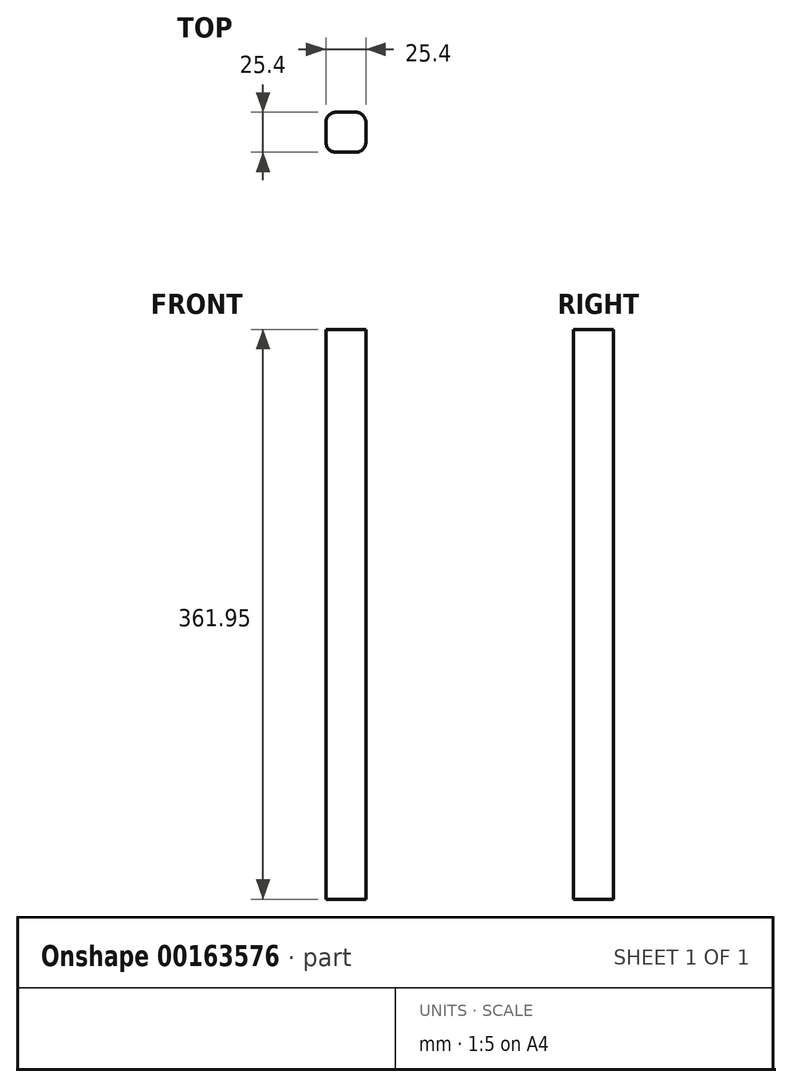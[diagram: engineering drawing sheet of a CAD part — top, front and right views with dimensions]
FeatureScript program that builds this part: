
annotation { "Feature Type Name" : "Feature", "Feature Type Description" : "" }
export const myFeature = defineFeature(function(context is Context, id is Id, definition is map)
    precondition{}
    {
        {
            var Q0;
            Q0=qCreatedBy(makeId("Top.planeOp"),FACE);
            var sketch = newSketch(context, id + "F0", { "sketchPlane" : qUnion([Q0])});
            skLineSegment(sketch, "E0.bottom", {"start": v(6.35, 12.7) * mm, "end": v(-6.35, 12.7) * mm});
            skLineSegment(sketch, "E0.top", {"start": v(6.35, -12.7) * mm, "end": v(-6.35, -12.7) * mm});
            skLineSegment(sketch, "E0.left", {"start": v(12.7, 6.35) * mm, "end": v(12.7, -6.35) * mm});
            skLineSegment(sketch, "E0.right", {"start": v(-12.7, 6.35) * mm, "end": v(-12.7, -6.35) * mm});
            skPoint(sketch, "E0.middle", {"position": v(0, 0) * mm});
            skPoint(sketch, "E1.visualSharp", {"position": v(-12.7, 12.7) * mm});
            skArc(sketch, "E1.filletArc", {"start": v(-6.35, 12.7) * mm, "mid": v(-10.84, 10.84) * mm, "end": v(-12.7, 6.35) * mm});
            skPoint(sketch, "E2.visualSharp", {"position": v(-12.7, -12.7) * mm});
            skArc(sketch, "E2.filletArc", {"start": v(-12.7, -6.35) * mm, "mid": v(-10.84, -10.84) * mm, "end": v(-6.35, -12.7) * mm});
            skPoint(sketch, "E3.visualSharp", {"position": v(12.7, -12.7) * mm});
            skArc(sketch, "E3.filletArc", {"start": v(6.35, -12.7) * mm, "mid": v(10.84, -10.84) * mm, "end": v(12.7, -6.35) * mm});
            skPoint(sketch, "E4.visualSharp", {"position": v(12.7, 12.7) * mm});
            skArc(sketch, "E4.filletArc", {"start": v(12.7, 6.35) * mm, "mid": v(10.84, 10.84) * mm, "end": v(6.35, 12.7) * mm});
            skSolve(sketch);
        }
        {
            var Q0;
            Q0=qSketchRegion(id+"F0",true);
            extrude(context, id + "F1", {"entities" : qUnion([Q0]), "depth" : 361.95 * mm, "offsetDistance" : 25.4 * mm});
        }
    });
